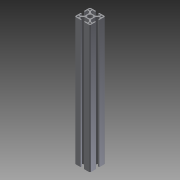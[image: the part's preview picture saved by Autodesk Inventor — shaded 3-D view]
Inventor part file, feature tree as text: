
AUTODESK INVENTOR PART (.ipt)
format: ipt  version: 2016 (Build 200138000, 138)  size: 216,576 bytes
history: native  units: mm
features: other x42, sketch x5, hole x4, extrude x1
ambient origin geometry x8: Origin, YZ Plane, XZ Plane, XY Plane, X Axis, Y Axis, Z Axis, Center Point
bodies: Solid1 (feature_tree)
feature tree (52):
  extrude  "Extrusion1"  [1 undecoded]
  hole  "Drilling 1"  [1 undecoded]
  hole  "Drilling 2"  [1 undecoded]
  hole  "Drilling 3"  [1 undecoded]
  hole  "Drilling 4"  [1 undecoded]
  other  "side_4d_XY"
  other  "side_4d_YZ"
  other  "side_4d_ZX"
  other  "side_4d_X"
  other  "side_4d_Y"
  other  "side_4d_Z"
  other  "side_4d_Center"
  other  "side_1a_XY"
  other  "side_1a_YZ"
  other  "side_1a_ZX"
  other  "side_1a_X"
  other  "side_1a_Y"
  other  "side_1a_Z"
  other  "side_1a_Center"
  other  "side_2b_XY"
  other  "side_2b_YZ"
  other  "side_2b_ZX"
  other  "side_2b_X"
  other  "side_2b_Y"
  other  "side_2b_Z"
  other  "side_2b_Center"
  other  "side_3c_XY"
  other  "side_3c_YZ"
  other  "side_3c_ZX"
  other  "side_3c_X"
  other  "side_3c_Y"
  other  "side_3c_Z"
  other  "side_3c_Center"
  other  "end_XY"
  other  "end_YZ"
  other  "end_ZX"
  other  "end_X"
  other  "end_Y"
  other  "end_Z"
  other  "end_Center"
  other  "start_XY"
  other  "start_YZ"
  other  "start_ZX"
  other  "start_X"
  other  "start_Y"
  other  "start_Z"
  other  "start_Center"
  sketch  "Skizze_1"  dims[d0=330.0mm d1=0.0mm]
  sketch  "Sketch2"  dims[d2=5.0mm d3=6.0mm d4=4.0mm d5=2.0mm d6=90.0deg d7=6000.0mm d8=0.0mm]
  sketch  "Sketch3"  dims[d9=5.0mm d10=6.0mm d11=4.0mm d12=2.0mm d13=90.0deg d14=6000.0mm d15=0.0mm]
  sketch  "Sketch4"  dims[d16=5.0mm d17=6.0mm d18=4.0mm d19=2.0mm d20=90.0deg d21=6000.0mm d22=0.0mm]
  sketch  "Sketch5"  dims[d23=5.0mm d24=6.0mm d25=4.0mm d26=2.0mm d27=90.0deg d28=6000.0mm d29=0.0mm]
note: 5 required parameter values undecoded (feature->parameter linkage not recoverable at this tier; creation-order binding heuristic only, values carry confidence <= 0.55)
